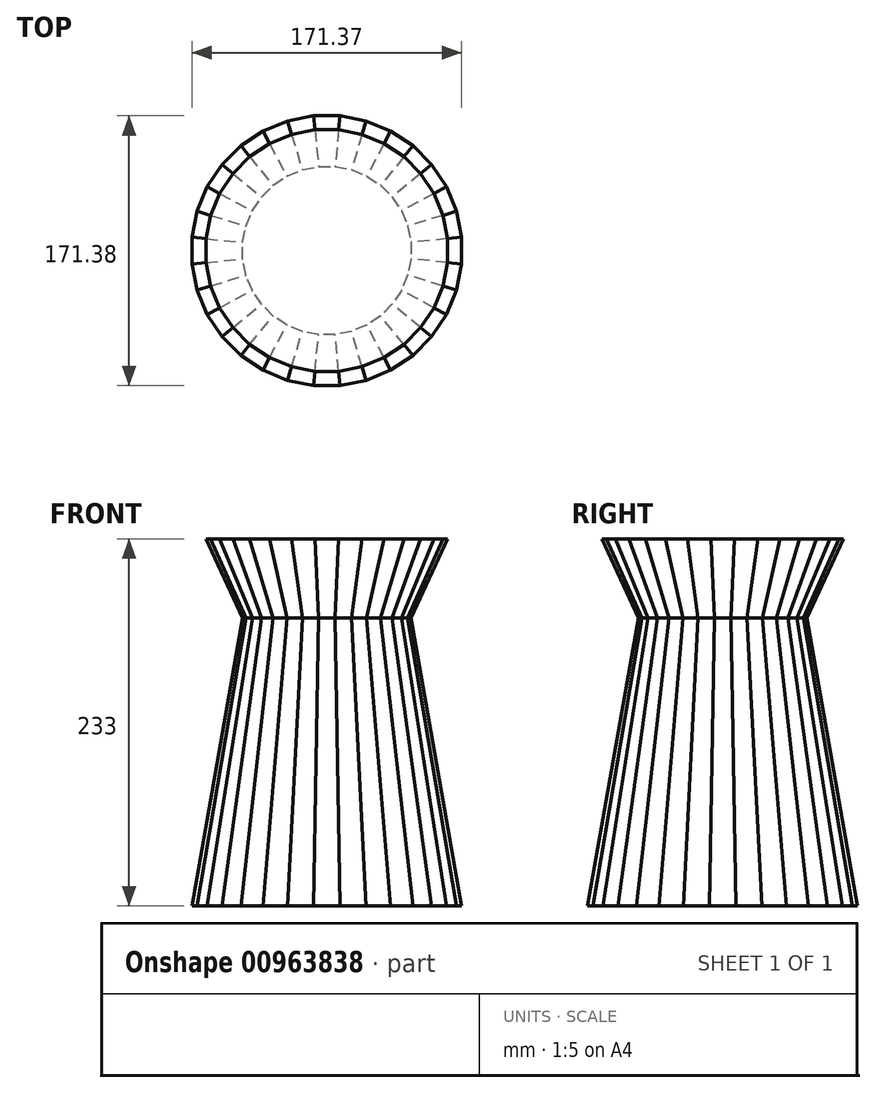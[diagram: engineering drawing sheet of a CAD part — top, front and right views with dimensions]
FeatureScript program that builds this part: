
annotation { "Feature Type Name" : "Feature", "Feature Type Description" : "" }
export const myFeature = defineFeature(function(context is Context, id is Id, definition is map)
    precondition{}
    {
        {
            var Q0;
            Q0=qCreatedBy(makeId("Top.planeOp"),FACE);
            var sketch = newSketch(context, id + "F0", { "sketchPlane" : qUnion([Q0])});
            skCircle(sketch, "E0.cCircle", {"center": v(-39.82, 0) * mm, "radius": 53.42 * mm, "construction": true});
            skLineSegment(sketch, "E0.0", {"start": v(13.6, 5.26) * mm, "end": v(13.6, -5.26) * mm});
            skLineSegment(sketch, "E0.1", {"start": v(13.6, -5.26) * mm, "end": v(11.55, -15.58) * mm});
            skLineSegment(sketch, "E0.2", {"start": v(11.55, -15.58) * mm, "end": v(7.52, -25.3) * mm});
            skLineSegment(sketch, "E0.3", {"start": v(7.52, -25.3) * mm, "end": v(1.68, -34.05) * mm});
            skLineSegment(sketch, "E0.4", {"start": v(1.68, -34.05) * mm, "end": v(-5.76, -41.5) * mm});
            skLineSegment(sketch, "E0.5", {"start": v(-5.76, -41.5) * mm, "end": v(-14.51, -47.34) * mm});
            skLineSegment(sketch, "E0.6", {"start": v(-14.51, -47.34) * mm, "end": v(-24.23, -51.37) * mm});
            skLineSegment(sketch, "E0.7", {"start": v(-24.23, -51.37) * mm, "end": v(-34.55, -53.42) * mm});
            skLineSegment(sketch, "E0.8", {"start": v(-34.55, -53.42) * mm, "end": v(-45.08, -53.42) * mm});
            skLineSegment(sketch, "E0.9", {"start": v(-45.08, -53.42) * mm, "end": v(-55.4, -51.37) * mm});
            skLineSegment(sketch, "E0.10", {"start": v(-55.4, -51.37) * mm, "end": v(-65.12, -47.34) * mm});
            skLineSegment(sketch, "E0.11", {"start": v(-65.12, -47.34) * mm, "end": v(-73.87, -41.5) * mm});
            skLineSegment(sketch, "E0.12", {"start": v(-73.87, -41.5) * mm, "end": v(-81.3, -34.05) * mm});
            skLineSegment(sketch, "E0.13", {"start": v(-81.3, -34.05) * mm, "end": v(-87.15, -25.3) * mm});
            skLineSegment(sketch, "E0.14", {"start": v(-87.15, -25.3) * mm, "end": v(-91.18, -15.58) * mm});
            skLineSegment(sketch, "E0.15", {"start": v(-91.18, -15.58) * mm, "end": v(-93.23, -5.26) * mm});
            skLineSegment(sketch, "E0.16", {"start": v(-93.23, -5.26) * mm, "end": v(-93.23, 5.26) * mm});
            skLineSegment(sketch, "E0.17", {"start": v(-93.23, 5.26) * mm, "end": v(-91.18, 15.58) * mm});
            skLineSegment(sketch, "E0.18", {"start": v(-91.18, 15.58) * mm, "end": v(-87.15, 25.3) * mm});
            skLineSegment(sketch, "E0.19", {"start": v(-87.15, 25.3) * mm, "end": v(-81.3, 34.05) * mm});
            skLineSegment(sketch, "E0.20", {"start": v(-81.3, 34.05) * mm, "end": v(-73.87, 41.5) * mm});
            skLineSegment(sketch, "E0.21", {"start": v(-73.87, 41.5) * mm, "end": v(-65.12, 47.34) * mm});
            skLineSegment(sketch, "E0.22", {"start": v(-65.12, 47.34) * mm, "end": v(-55.4, 51.37) * mm});
            skLineSegment(sketch, "E0.23", {"start": v(-55.4, 51.37) * mm, "end": v(-45.08, 53.42) * mm});
            skLineSegment(sketch, "E0.24", {"start": v(-45.08, 53.42) * mm, "end": v(-34.55, 53.42) * mm});
            skLineSegment(sketch, "E0.25", {"start": v(-34.55, 53.42) * mm, "end": v(-24.23, 51.37) * mm});
            skLineSegment(sketch, "E0.26", {"start": v(-24.23, 51.37) * mm, "end": v(-14.51, 47.34) * mm});
            skLineSegment(sketch, "E0.27", {"start": v(-14.51, 47.34) * mm, "end": v(-5.76, 41.5) * mm});
            skLineSegment(sketch, "E0.28", {"start": v(-5.76, 41.5) * mm, "end": v(1.68, 34.05) * mm});
            skLineSegment(sketch, "E0.29", {"start": v(1.68, 34.05) * mm, "end": v(7.52, 25.3) * mm});
            skLineSegment(sketch, "E0.30", {"start": v(7.52, 25.3) * mm, "end": v(11.55, 15.58) * mm});
            skLineSegment(sketch, "E0.31", {"start": v(11.55, 15.58) * mm, "end": v(13.6, 5.26) * mm});
            skPoint(sketch, "E0.0.midPoint", {"position": v(13.6, 0) * mm});
            skSolve(sketch);
        }
        {
            var Q0;
            Q0 = qSketchRegion(id + "F0", true);
            extrude(context, id + "F1", {"entities" : qUnion([Q0]), "depth" : 50 * mm, "offsetDistance" : 25 * mm, "hasDraft" : true, "draftAngle" : 25 * degree, "hasSecondDirection" : true, "secondDirectionOppositeDirection" : true, "secondDirectionDepth" : 183 * mm, "hasSecondDirectionDraft" : true, "secondDirectionDraftAngle" : 10 * degree});
        }
    });
